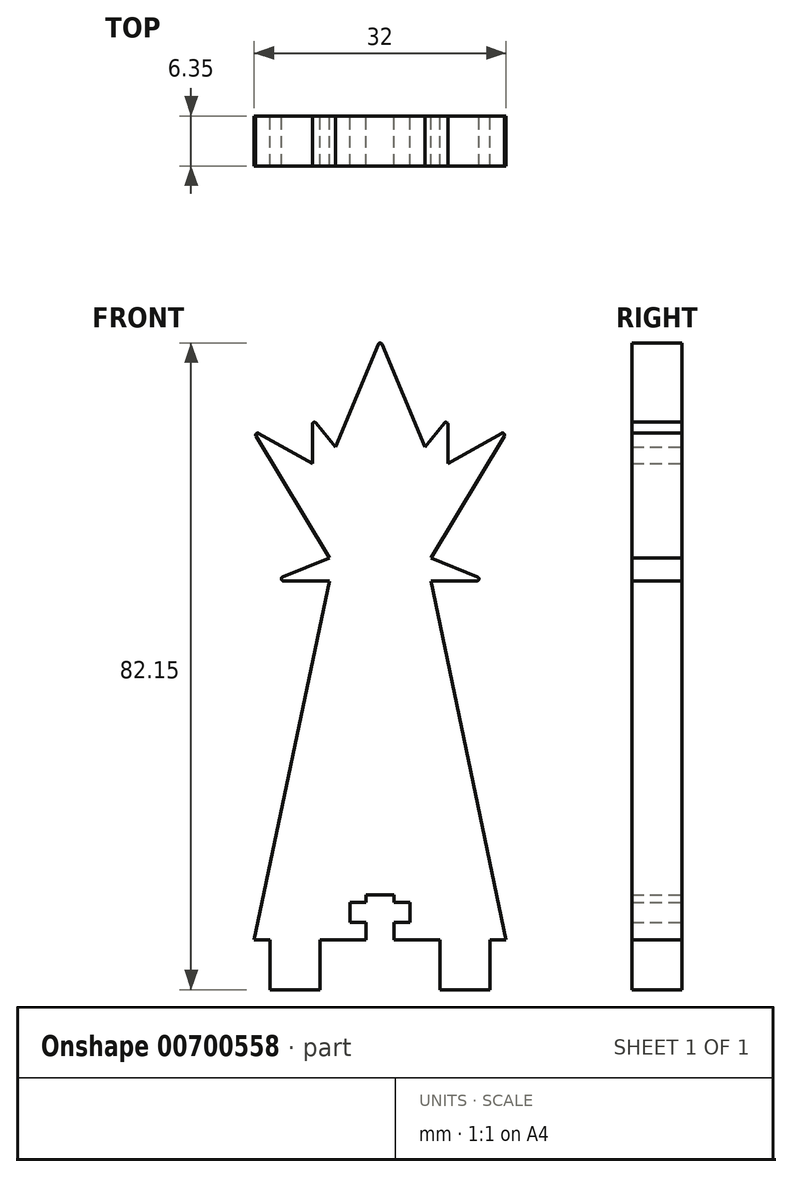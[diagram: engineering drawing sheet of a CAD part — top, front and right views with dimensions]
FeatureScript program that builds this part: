
annotation { "Feature Type Name" : "Feature", "Feature Type Description" : "" }
export const myFeature = defineFeature(function(context is Context, id is Id, definition is map)
    precondition{}
    {
        {
            var Q0;
            Q0=qCreatedBy(makeId("Front.planeOp"),FACE);
            var sketch = newSketch(context, id + "F0", { "sketchPlane" : qUnion([Q0])});
            skLineSegment(sketch, "E0", {"start": v(-13.97, 0) * mm, "end": v(-13.97, -6.35) * mm});
            skLineSegment(sketch, "E1", {"start": v(-13.97, -6.35) * mm, "end": v(-7.62, -6.35) * mm});
            skLineSegment(sketch, "E2", {"start": v(-7.62, -6.35) * mm, "end": v(-7.62, 0) * mm});
            skLineSegment(sketch, "E3", {"start": v(-7.62, 0) * mm, "end": v(7.62, 0) * mm});
            skLineSegment(sketch, "E4", {"start": v(-13.97, 0) * mm, "end": v(-16, 0) * mm});
            skLineSegment(sketch, "E5", {"start": v(-16, 0) * mm, "end": v(-6.44, 45.58) * mm});
            skLineSegment(sketch, "E6", {"start": v(-6.44, 45.58) * mm, "end": v(-12.3, 45.58) * mm});
            skLineSegment(sketch, "E7", {"start": v(-12.4, 46.07) * mm, "end": v(-6.44, 48.46) * mm});
            skLineSegment(sketch, "E8", {"start": v(-6.44, 48.46) * mm, "end": v(-15.77, 63.98) * mm});
            skLineSegment(sketch, "E9", {"start": v(-15.43, 64.33) * mm, "end": v(-7.2, 59.7) * mm});
            skLineSegment(sketch, "E10", {"start": v(-6.85, 59.82) * mm, "end": v(-0.23, 75.64) * mm});
            skPoint(sketch, "E11.visualSharp", {"position": v(-6.96, 59.56) * mm});
            skArc(sketch, "E11.filletArc", {"start": v(-6.88, 60.07) * mm, "mid": v(-6.88, 60.07) * mm, "end": v(-6.89, 60.08) * mm});
            skArc(sketch, "E12.MirrorCS", {"start": v(6.88, 60.07) * mm, "mid": v(6.88, 60.07) * mm, "end": v(6.89, 60.08) * mm});
            skLineSegment(sketch, "E13.MirrorCS", {"start": v(13.97, 0) * mm, "end": v(16, 0) * mm});
            skLineSegment(sketch, "E14.MirrorCS", {"start": v(7.62, -6.35) * mm, "end": v(7.62, 0) * mm});
            skLineSegment(sketch, "E15.MirrorCS", {"start": v(16, 0) * mm, "end": v(6.44, 45.58) * mm});
            skLineSegment(sketch, "E16.MirrorCS", {"start": v(6.44, 45.58) * mm, "end": v(12.3, 45.58) * mm});
            skLineSegment(sketch, "E17.MirrorCS", {"start": v(13.97, -6.35) * mm, "end": v(7.62, -6.35) * mm});
            skLineSegment(sketch, "E18.MirrorCS", {"start": v(12.4, 46.07) * mm, "end": v(6.44, 48.46) * mm});
            skLineSegment(sketch, "E19.MirrorCS", {"start": v(6.44, 48.46) * mm, "end": v(15.77, 63.98) * mm});
            skLineSegment(sketch, "E20.MirrorCS", {"start": v(15.43, 64.33) * mm, "end": v(7.2, 59.7) * mm});
            skLineSegment(sketch, "E21.MirrorCS", {"start": v(13.97, 0) * mm, "end": v(13.97, -6.35) * mm});
            skLineSegment(sketch, "E22.MirrorCS", {"start": v(7.62, 0) * mm, "end": v(-7.62, 0) * mm});
            skLineSegment(sketch, "E23.MirrorCS", {"start": v(6.85, 59.82) * mm, "end": v(0.23, 75.64) * mm});
            skPoint(sketch, "E24.MirrorP", {"position": v(6.96, 59.56) * mm});
            skPoint(sketch, "E25.newPointA", {"position": v(-4.82, 58.35) * mm});
            skPoint(sketch, "E25.newPointB", {"position": v(-6.26, 61.23) * mm});
            skArc(sketch, "E25.filletArc", {"start": v(-7.2, 59.7) * mm, "mid": v(-7, 59.68) * mm, "end": v(-6.85, 59.82) * mm});
            skPoint(sketch, "E26.newPointA", {"position": v(6.26, 61.23) * mm});
            skPoint(sketch, "E26.newPointB", {"position": v(4.82, 58.35) * mm});
            skArc(sketch, "E26.filletArc", {"start": v(6.85, 59.82) * mm, "mid": v(7, 59.68) * mm, "end": v(7.2, 59.7) * mm});
            skPoint(sketch, "E27.visualSharp", {"position": v(0, 76.2) * mm});
            skArc(sketch, "E27.filletArc", {"start": v(0.23, 75.64) * mm, "mid": v(0, 75.8) * mm, "end": v(-0.23, 75.64) * mm});
            skPoint(sketch, "E28.visualSharp", {"position": v(-16.27, 64.8) * mm});
            skArc(sketch, "E28.filletArc", {"start": v(-15.43, 64.33) * mm, "mid": v(-15.73, 64.28) * mm, "end": v(-15.77, 63.98) * mm});
            skPoint(sketch, "E29.visualSharp", {"position": v(16.27, 64.8) * mm});
            skArc(sketch, "E29.filletArc", {"start": v(15.77, 63.98) * mm, "mid": v(15.73, 64.28) * mm, "end": v(15.43, 64.33) * mm});
            skPoint(sketch, "E30.visualSharp", {"position": v(-13.6, 45.58) * mm});
            skArc(sketch, "E30.filletArc", {"start": v(-12.4, 46.07) * mm, "mid": v(-12.54, 45.78) * mm, "end": v(-12.3, 45.58) * mm});
            skPoint(sketch, "E31.visualSharp", {"position": v(13.6, 45.58) * mm});
            skArc(sketch, "E31.filletArc", {"start": v(12.3, 45.58) * mm, "mid": v(12.54, 45.78) * mm, "end": v(12.4, 46.07) * mm});
            skLineSegment(sketch, "E32", {"start": v(-8.6, 60.48) * mm, "end": v(-8.6, 65.47) * mm});
            skLineSegment(sketch, "E33", {"start": v(-8.15, 65.63) * mm, "end": v(-5.7, 62.57) * mm});
            skLineSegment(sketch, "E34.MirrorCS", {"start": v(8.6, 60.48) * mm, "end": v(8.6, 65.47) * mm});
            skArc(sketch, "E35.MirrorCS", {"start": v(-6.85, 59.82) * mm, "mid": v(-7, 59.68) * mm, "end": v(-7.2, 59.7) * mm});
            skArc(sketch, "E36.MirrorCS", {"start": v(7.2, 59.7) * mm, "mid": v(7, 59.68) * mm, "end": v(6.85, 59.82) * mm});
            skArc(sketch, "E37.MirrorCS", {"start": v(-0.23, 75.64) * mm, "mid": v(0, 75.8) * mm, "end": v(0.23, 75.64) * mm});
            skArc(sketch, "E38.MirrorCS", {"start": v(12.4, 46.07) * mm, "mid": v(12.54, 45.78) * mm, "end": v(12.3, 45.58) * mm});
            skArc(sketch, "E39.MirrorCS", {"start": v(-12.3, 45.58) * mm, "mid": v(-12.54, 45.78) * mm, "end": v(-12.4, 46.07) * mm});
            skArc(sketch, "E40.MirrorCS", {"start": v(15.43, 64.33) * mm, "mid": v(15.73, 64.28) * mm, "end": v(15.77, 63.98) * mm});
            skArc(sketch, "E41.MirrorCS", {"start": v(-15.77, 63.98) * mm, "mid": v(-15.73, 64.28) * mm, "end": v(-15.43, 64.33) * mm});
            skLineSegment(sketch, "E42.MirrorCS", {"start": v(8.15, 65.63) * mm, "end": v(5.7, 62.57) * mm});
            skLineSegment(sketch, "E43.MirrorCS", {"start": v(8.6, 60.48) * mm, "end": v(8.6, 66.2) * mm});
            skLineSegment(sketch, "E44.MirrorCS", {"start": v(-8.6, 60.48) * mm, "end": v(-8.6, 66.2) * mm});
            skPoint(sketch, "E45.visualSharp", {"position": v(-8.6, 66.2) * mm});
            skArc(sketch, "E45.filletArc", {"start": v(-8.15, 65.63) * mm, "mid": v(-8.43, 65.71) * mm, "end": v(-8.6, 65.47) * mm});
            skPoint(sketch, "E46.visualSharp", {"position": v(8.6, 66.2) * mm});
            skArc(sketch, "E46.filletArc", {"start": v(8.6, 65.47) * mm, "mid": v(8.43, 65.71) * mm, "end": v(8.15, 65.63) * mm});
            skSolve(sketch);
        }
        {
            var Q0;
            {var subQ0=sQuery(id+"F0.wireOp",EDGE,"E26.filletArc");var subQ9=sQuery(id+"F0.wireOp",EDGE,"E25.filletArc");var subQ21=makeQuery(id+"F0.imprint","IMPRINT",EDGE,{"derivedFrom":subQ9});var subQ22=makeQuery(id+"F0.imprint","IMPRINT",EDGE,{"derivedFrom":subQ0});Q0=qUnion([makeQuery(id+"F0.imprint","IMPRINT",FACE,{"disambiguationData":[TD([[subQ21,1.0]])]}),makeQuery(id+"F0.imprint","IMPRINT",FACE,{"disambiguationData":[TD([[subQ22,1.0]])]}),makeQuery(id+"F0.imprint","IMPRINT",FACE,{"disambiguationData":[TD([[makeQuery(id+"F0.imprint","IMPRINT",EDGE,{"derivedFrom":sQuery(id+"F0.wireOp",EDGE,"E0")}),1.0]])]})]);}
            extrude(context, id + "F1", {"entities" : qUnion([Q0]), "depth" : 6.35 * mm, "offsetDistance" : 25.4 * mm});
        }
        {
            var Q0;
            Q0=qCreatedBy(makeId("Front.planeOp"),FACE);
            var sketch = newSketch(context, id + "F2", { "sketchPlane" : qUnion([Q0])});
            skLineSegment(sketch, "E47", {"start": v(-42.07, 27.06) * mm, "end": v(-42.07, 27.06) * mm});
            skLineSegment(sketch, "E48.bottom", {"start": v(-1.78, 5.72) * mm, "end": v(1.78, 5.72) * mm});
            skLineSegment(sketch, "E48.left", {"start": v(-1.78, 5.72) * mm, "end": v(-1.78, 4.76) * mm});
            skLineSegment(sketch, "E49", {"start": v(0, 5.72) * mm, "end": v(0, 9.6) * mm, "construction": true});
            skLineSegment(sketch, "E50.bottom", {"start": v(-1.78, 4.76) * mm, "end": v(-3.81, 4.76) * mm});
            skLineSegment(sketch, "E50.top", {"start": v(-1.78, 2.22) * mm, "end": v(-3.81, 2.22) * mm});
            skLineSegment(sketch, "E50.right", {"start": v(-3.81, 4.76) * mm, "end": v(-3.81, 2.22) * mm});
            skLineSegment(sketch, "E51.top", {"start": v(-1.78, 0) * mm, "end": v(1.78, 0) * mm});
            skLineSegment(sketch, "E51.left", {"start": v(-1.78, 2.22) * mm, "end": v(-1.78, 0) * mm});
            skLineSegment(sketch, "E52.MirrorCS", {"start": v(3.8, 4.76) * mm, "end": v(3.8, 2.22) * mm});
            skLineSegment(sketch, "E53.MirrorCS", {"start": v(1.78, 5.72) * mm, "end": v(1.78, 4.76) * mm});
            skLineSegment(sketch, "E54.MirrorCS", {"start": v(1.78, 2.22) * mm, "end": v(1.78, 0) * mm});
            skLineSegment(sketch, "E55.MirrorCS", {"start": v(1.78, 4.76) * mm, "end": v(3.8, 4.76) * mm});
            skLineSegment(sketch, "E56.MirrorCS", {"start": v(1.78, 0) * mm, "end": v(-1.78, 0) * mm});
            skLineSegment(sketch, "E57.MirrorCS", {"start": v(1.78, 2.22) * mm, "end": v(3.8, 2.22) * mm});
            skLineSegment(sketch, "E58.MirrorCS", {"start": v(1.78, 5.72) * mm, "end": v(-1.78, 5.72) * mm});
            skSolve(sketch);
        }
        {
            var Q0;
            Q0 = qSketchRegion(id + "F2", true);
            extrude(context, id + "F3", {"entities" : qUnion([Q0]), "operationType" : NewBodyOperationType.REMOVE, "depth" : 25.4 * mm, "offsetDistance" : 25.4 * mm});
        }
    });
